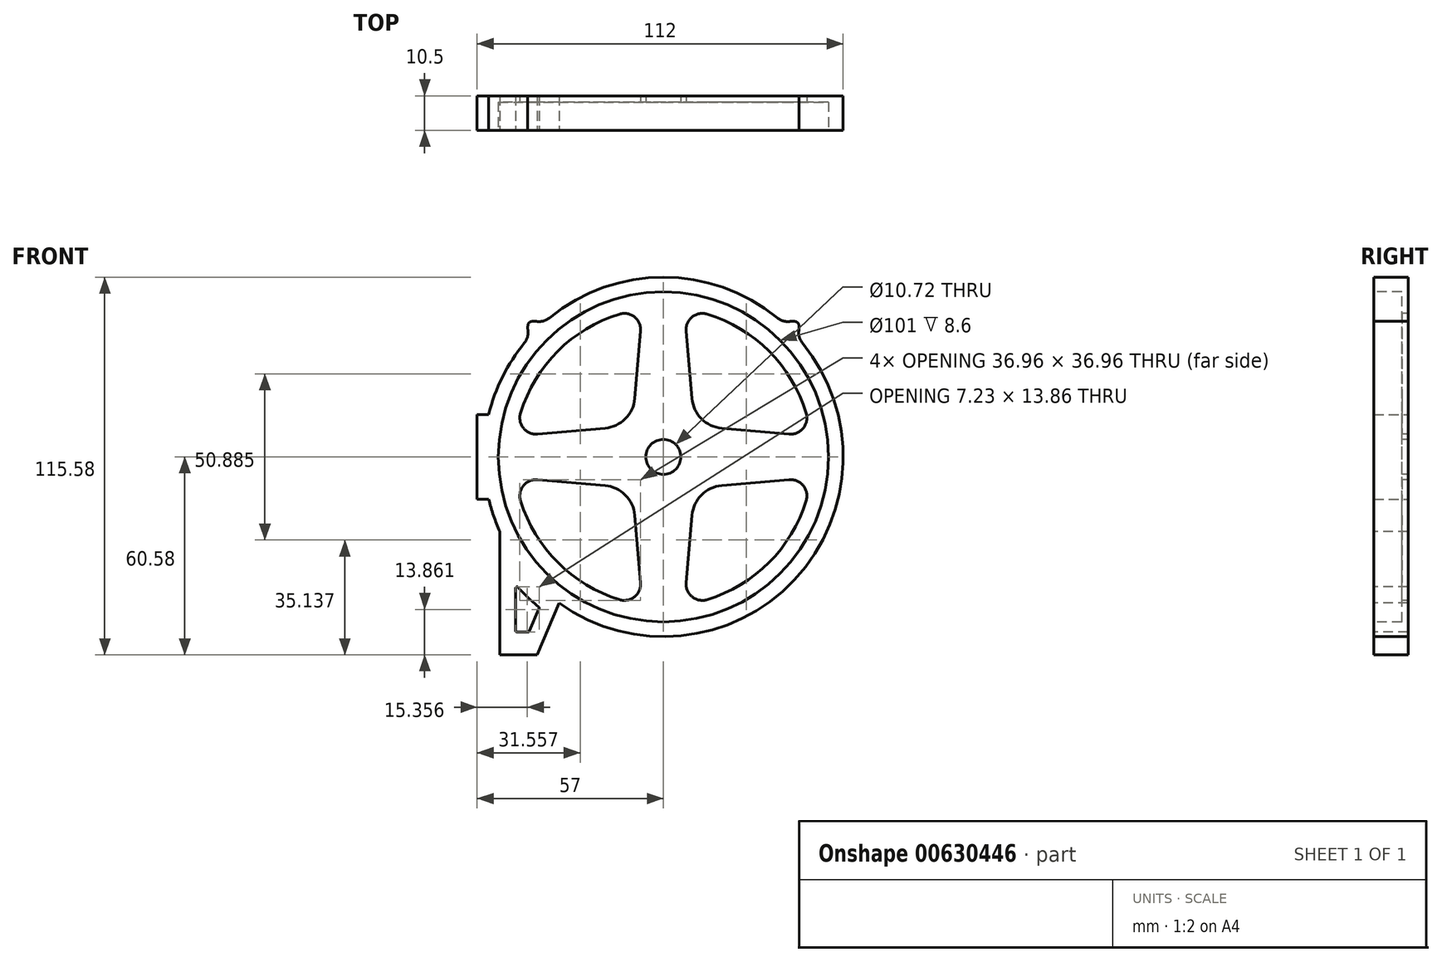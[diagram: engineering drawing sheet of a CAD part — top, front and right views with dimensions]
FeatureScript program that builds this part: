
annotation { "Feature Type Name" : "Feature", "Feature Type Description" : "" }
export const myFeature = defineFeature(function(context is Context, id is Id, definition is map)
    precondition{}
    {
        {
            var Q0;
            Q0=qCreatedBy(makeId("Front.planeOp"),FACE);
            var sketch = newSketch(context, id + "F0", { "sketchPlane" : qUnion([Q0])});
            skCircle(sketch, "E0", {"center": v(0, 0) * mm, "radius": 50.5 * mm});
            skArc(sketch, "E1", {"start": v(-53.44, -13) * mm, "mid": v(55, 0) * mm, "end": v(-53.44, 13) * mm});
            skLineSegment(sketch, "E2", {"start": v(0, 0) * mm, "end": v(55.3, 55.3) * mm});
            skLineSegment(sketch, "E3.trimOffspring", {"start": v(-38.9, 38.9) * mm, "end": v(-41.08, 41.08) * mm});
            skFitSpline(sketch, "E4", {"points": [v(-41.08, 36.57) * mm, v(-41.08, 41.08) * mm, v(-36.57, 41.08) * mm], "startDerivative": vector(-2.26, 11.29) * mm, "endDerivative": vector(11.29, -2.26) * mm});
            skFitSpline(sketch, "E5.MirrorCS", {"points": [v(41.08, 36.57) * mm, v(41.08, 41.08) * mm, v(36.57, 41.08) * mm], "startDerivative": vector(2.26, 11.29) * mm, "endDerivative": vector(-11.29, -2.26) * mm});
            skLineSegment(sketch, "E6.0", {"start": v(-57, -13) * mm, "end": v(-57, 0) * mm});
            skLineSegment(sketch, "E7.0", {"start": v(-57, 13) * mm, "end": v(-53.44, 13) * mm});
            skPoint(sketch, "E8.orphan", {"position": v(-50.5, 0) * mm});
            skLineSegment(sketch, "E9.MirrorCS", {"start": v(-57, -13) * mm, "end": v(-53.44, -13) * mm});
            skLineSegment(sketch, "E10", {"start": v(-57, 0) * mm, "end": v(-57, 13) * mm});
            skSolve(sketch);
        }
        {
            var Q0;
            Q0=makeQuery(id+"F0.imprint","IMPRINT",FACE,{"disambiguationData":[TD([[makeQuery(id+"F0.imprint","IMPRINT",EDGE,{"derivedFrom":sQuery(id+"F0.wireOp",EDGE,"E0")}),-1.0]])]});
            var Q1;
            {var subQ0=sQuery(id+"F0.wireOp",EDGE,"E3.trimOffspring");Q1=makeQuery(id+"F0.imprint","IMPRINT",FACE,{"disambiguationData":[TD([[makeQuery(id+"F0.imprint","IMPRINT",EDGE,{"derivedFrom":subQ0}),1.0]])]});}
            var Q2;
            {var subQ0=sQuery(id+"F0.wireOp",EDGE,"E3.trimOffspring");Q2=makeQuery(id+"F0.imprint","IMPRINT",FACE,{"disambiguationData":[TD([[makeQuery(id+"F0.imprint","IMPRINT",EDGE,{"derivedFrom":subQ0}),-1.0]])]});}
            var Q3;
            {var subQ0=sQuery(id+"F0.wireOp",EDGE,"E5.MirrorCS");var subQ1=sQuery(id+"F0.wireOp",EDGE,"E1");var subQ2=makeQuery(id+"F0.imprint","INTERSECT",VERTEX,{"disambiguationData":[OD(1.0)],"derivedFrom":[subQ1,subQ0]});Q3=makeQuery(id+"F0.imprint","IMPRINT",FACE,{"disambiguationData":[TD([[makeQuery(id+"F0.imprint","IMPRINT",EDGE,{"disambiguationData":[TD([[subQ2,1.0]])],"derivedFrom":subQ1}),-1.0]])]});}
            var Q4;
            {var subQ0=sQuery(id+"F0.wireOp",EDGE,"E5.MirrorCS");var subQ1=sQuery(id+"F0.wireOp",EDGE,"E1");var subQ2=makeQuery(id+"F0.imprint","INTERSECT",VERTEX,{"disambiguationData":[OD(0.0)],"derivedFrom":[subQ1,subQ0]});Q4=makeQuery(id+"F0.imprint","IMPRINT",FACE,{"disambiguationData":[TD([[makeQuery(id+"F0.imprint","IMPRINT",EDGE,{"disambiguationData":[TD([[subQ2,-1.0]])],"derivedFrom":subQ1}),-1.0]])]});}
            extrude(context, id + "F1", {"entities" : qUnion([Q0, Q1, Q2, Q3, Q4]), "depth" : 10.5 * mm, "offsetDistance" : 25 * mm});
        }
        {
            var Q0;
            {var subQ0=sQuery(id+"F0.wireOp",EDGE,"E4");var subQ1=sQuery(id+"F0.wireOp",EDGE,"E1");Q0=makeQuery(id+"F1.opExtrude","SWEPT_EDGE",EDGE,{"disambiguationData":[OSD([subQ1,subQ0]),TDD([makeQuery(id+"F0.imprint","INTERSECT",VERTEX,{"disambiguationData":[OD(0.0)],"derivedFrom":[subQ1,subQ0]})])]});}
            var Q1;
            {var subQ0=sQuery(id+"F0.wireOp",EDGE,"E4");var subQ1=sQuery(id+"F0.wireOp",EDGE,"E1");Q1=makeQuery(id+"F1.opExtrude","SWEPT_EDGE",EDGE,{"disambiguationData":[OSD([subQ1,subQ0]),TDD([makeQuery(id+"F0.imprint","INTERSECT",VERTEX,{"disambiguationData":[OD(1.0)],"derivedFrom":[subQ1,subQ0]})])]});}
            var Q2;
            {var subQ0=sQuery(id+"F0.wireOp",EDGE,"E5.MirrorCS");var subQ1=sQuery(id+"F0.wireOp",EDGE,"E1");Q2=makeQuery(id+"F1.opExtrude","SWEPT_EDGE",EDGE,{"disambiguationData":[OSD([subQ1,subQ0]),TDD([makeQuery(id+"F0.imprint","INTERSECT",VERTEX,{"disambiguationData":[OD(1.0)],"derivedFrom":[subQ1,subQ0]})])]});}
            var Q3;
            {var subQ0=sQuery(id+"F0.wireOp",EDGE,"E5.MirrorCS");var subQ1=sQuery(id+"F0.wireOp",EDGE,"E1");Q3=makeQuery(id+"F1.opExtrude","SWEPT_EDGE",EDGE,{"disambiguationData":[OSD([subQ1,subQ0]),TDD([makeQuery(id+"F0.imprint","INTERSECT",VERTEX,{"disambiguationData":[OD(0.0)],"derivedFrom":[subQ1,subQ0]})])]});}
            fillet(context, id + "F2", {"entities" : qUnion([Q0, Q1, Q2, Q3]), "radius" : 5 * mm, "tangentPropagation" : true, "allowEdgeOverflow" : false});
        }
        {
            var Q0;
            Q0=makeQuery(id+"F1.opExtrude","CAP_FACE",FACE,{"disambiguationData":[OSD([sQuery(id+"F0.wireOp",EDGE,"E0"),sQuery(id+"F0.wireOp",EDGE,"E1"),sQuery(id+"F0.wireOp",EDGE,"E4"),sQuery(id+"F0.wireOp",EDGE,"E5.MirrorCS"),sQuery(id+"F0.wireOp",EDGE,"E6.0"),sQuery(id+"F0.wireOp",EDGE,"E7.0"),sQuery(id+"F0.wireOp",EDGE,"E9.MirrorCS"),sQuery(id+"F0.wireOp",EDGE,"E10")])],"isStart":false});
            var sketch = newSketch(context, id + "F3", { "sketchPlane" : qUnion([Q0])});
            skCircle(sketch, "E11", {"center": v(0, 0) * mm, "radius": 5.36 * mm});
            skSolve(sketch);
        }
        {
            var Q0;
            Q0=makeQuery(id+"F3.imprint","IMPRINT",FACE,{"disambiguationData":[TD([[makeQuery(id+"F3.imprint","IMPRINT",EDGE,{"derivedFrom":sQuery(id+"F3.wireOp",EDGE,"E11")}),-1.0]])]});
            var Q1;
            Q1=makeQuery(id+"F1.opExtrude","CAP_FACE",FACE,{"disambiguationData":[OSD([sQuery(id+"F0.wireOp",EDGE,"E0"),sQuery(id+"F0.wireOp",EDGE,"E1"),sQuery(id+"F0.wireOp",EDGE,"E4"),sQuery(id+"F0.wireOp",EDGE,"E5.MirrorCS"),sQuery(id+"F0.wireOp",EDGE,"E6.0"),sQuery(id+"F0.wireOp",EDGE,"E7.0"),sQuery(id+"F0.wireOp",EDGE,"E9.MirrorCS"),sQuery(id+"F0.wireOp",EDGE,"E10")])],"isStart":true});
            extrude(context, id + "F4", {"entities" : qUnion([Q0]), "operationType" : NewBodyOperationType.ADD, "endBound" : BoundingType.UP_TO_SURFACE, "oppositeDirection" : true, "depth" : 25 * mm, "endBoundEntityFace" : qUnion([Q1]), "offsetDistance" : 25 * mm});
        }
        {
            var Q0;
            {var subQ0=sQuery(id+"F0.wireOp",EDGE,"E0");Q0=makeQuery(id+"F4.boolean.opBoolean","MERGE",FACE,{"derivedFrom":[makeQuery(id+"F1.opExtrude","CAP_FACE",FACE,{"disambiguationData":[OSD([subQ0,sQuery(id+"F0.wireOp",EDGE,"E1"),sQuery(id+"F0.wireOp",EDGE,"E4"),sQuery(id+"F0.wireOp",EDGE,"E5.MirrorCS"),sQuery(id+"F0.wireOp",EDGE,"E6.0"),sQuery(id+"F0.wireOp",EDGE,"E7.0"),sQuery(id+"F0.wireOp",EDGE,"E9.MirrorCS"),sQuery(id+"F0.wireOp",EDGE,"E10")])],"isStart":false}),makeQuery(id+"F4.opExtrude","CAP_FACE",FACE,{"disambiguationData":[OSD([subQ0,sQuery(id+"F3.wireOp",EDGE,"E11")])],"isStart":true})]});}
            var sketch = newSketch(context, id + "F5", { "sketchPlane" : qUnion([Q0])});
            skLineSegment(sketch, "E12.0", {"start": v(-62, -18) * mm, "end": v(-57.24, -18) * mm});
            skLineSegment(sketch, "E12.1", {"start": v(-62, 18) * mm, "end": v(-62, -18) * mm});
            skArc(sketch, "E12.2", {"start": v(-57.24, -18) * mm, "mid": v(28.53, -52.78) * mm, "end": v(46.41, 38.03) * mm});
            skLineSegment(sketch, "E12.3", {"start": v(-57.24, 18) * mm, "end": v(-62, 18) * mm});
            skFitSpline(sketch, "E12.4", {"points": [v(45.99, 35.59) * mm, v(46.03, 35.82) * mm, v(46.13, 36.32) * mm, v(46.28, 37.12) * mm, v(46.41, 37.98) * mm, v(46.5, 38.93) * mm, v(46.53, 40) * mm, v(46.43, 41.08) * mm, v(46.17, 42.08) * mm, v(45.85, 42.9) * mm, v(45.44, 43.63) * mm, v(45, 44.2) * mm, v(44.62, 44.62) * mm, v(44.2, 45) * mm, v(43.63, 45.44) * mm, v(42.9, 45.85) * mm, v(42.08, 46.17) * mm, v(41.08, 46.43) * mm, v(40, 46.53) * mm, v(38.93, 46.5) * mm, v(37.98, 46.41) * mm, v(37.12, 46.28) * mm, v(36.32, 46.13) * mm, v(35.82, 46.03) * mm, v(35.59, 45.99) * mm]});
            skArc(sketch, "E12.5", {"start": v(38.03, 46.41) * mm, "mid": v(0, 60) * mm, "end": v(-38.03, 46.41) * mm});
            skFitSpline(sketch, "E12.6", {"points": [v(-35.59, 45.99) * mm, v(-35.82, 46.03) * mm, v(-36.32, 46.13) * mm, v(-37.12, 46.28) * mm, v(-37.98, 46.41) * mm, v(-38.93, 46.5) * mm, v(-40, 46.53) * mm, v(-41.08, 46.43) * mm, v(-42.08, 46.17) * mm, v(-42.9, 45.85) * mm, v(-43.63, 45.44) * mm, v(-44.2, 45) * mm, v(-44.62, 44.62) * mm, v(-45, 44.2) * mm, v(-45.44, 43.63) * mm, v(-45.85, 42.9) * mm, v(-46.17, 42.08) * mm, v(-46.43, 41.08) * mm, v(-46.53, 40) * mm, v(-46.5, 38.93) * mm, v(-46.41, 37.98) * mm, v(-46.28, 37.12) * mm, v(-46.13, 36.32) * mm, v(-46.03, 35.82) * mm, v(-45.99, 35.59) * mm]});
            skArc(sketch, "E12.7", {"start": v(-46.41, 38.03) * mm, "mid": v(-52.78, 28.53) * mm, "end": v(-57.24, 18) * mm});
            skFitSpline(sketch, "E13.4", {"points": [v(45.99, 35.59) * mm, v(46.03, 35.82) * mm, v(46.13, 36.32) * mm, v(46.28, 37.12) * mm, v(46.41, 37.98) * mm, v(46.5, 38.93) * mm, v(46.53, 40) * mm, v(46.43, 41.08) * mm, v(46.17, 42.08) * mm, v(45.85, 42.9) * mm, v(45.44, 43.63) * mm, v(45, 44.2) * mm, v(44.62, 44.62) * mm, v(44.2, 45) * mm, v(43.63, 45.44) * mm, v(42.9, 45.85) * mm, v(42.08, 46.17) * mm, v(41.08, 46.43) * mm, v(40, 46.53) * mm, v(38.93, 46.5) * mm, v(37.98, 46.41) * mm, v(37.12, 46.28) * mm, v(36.32, 46.13) * mm, v(35.82, 46.03) * mm, v(35.59, 45.99) * mm]});
            skFitSpline(sketch, "E13.6", {"points": [v(-35.59, 45.99) * mm, v(-35.82, 46.03) * mm, v(-36.32, 46.13) * mm, v(-37.12, 46.28) * mm, v(-37.98, 46.41) * mm, v(-38.93, 46.5) * mm, v(-40, 46.53) * mm, v(-41.08, 46.43) * mm, v(-42.08, 46.17) * mm, v(-42.9, 45.85) * mm, v(-43.63, 45.44) * mm, v(-44.2, 45) * mm, v(-44.62, 44.62) * mm, v(-45, 44.2) * mm, v(-45.44, 43.63) * mm, v(-45.85, 42.9) * mm, v(-46.17, 42.08) * mm, v(-46.43, 41.08) * mm, v(-46.53, 40) * mm, v(-46.5, 38.93) * mm, v(-46.41, 37.98) * mm, v(-46.28, 37.12) * mm, v(-46.13, 36.32) * mm, v(-46.03, 35.82) * mm, v(-45.99, 35.59) * mm]});
            skLineSegment(sketch, "E14", {"start": v(-9.5, 9.5) * mm, "end": v(-6.37, 45.27) * mm});
            skLineSegment(sketch, "E15", {"start": v(-9.5, 9.5) * mm, "end": v(-45.27, 6.37) * mm});
            skLineSegment(sketch, "E16.MirrorCS", {"start": v(9.5, 9.5) * mm, "end": v(45.27, 6.37) * mm});
            skLineSegment(sketch, "E17.MirrorCS", {"start": v(9.5, 9.5) * mm, "end": v(6.37, 45.27) * mm});
            skLineSegment(sketch, "E18.MirrorCS", {"start": v(-9.5, -9.5) * mm, "end": v(-6.37, -45.27) * mm});
            skLineSegment(sketch, "E19.MirrorCS", {"start": v(-9.5, -9.5) * mm, "end": v(-45.27, -6.37) * mm});
            skLineSegment(sketch, "E20.MirrorCS", {"start": v(9.5, -9.5) * mm, "end": v(45.27, -6.37) * mm});
            skLineSegment(sketch, "E21.MirrorCS", {"start": v(9.5, -9.5) * mm, "end": v(6.37, -45.27) * mm});
            skArc(sketch, "E22", {"start": v(-6.37, 45.27) * mm, "mid": v(-32.33, 32.33) * mm, "end": v(-45.27, 6.37) * mm});
            skArc(sketch, "E23.trimOffspring", {"start": v(-45.27, -6.37) * mm, "mid": v(-32.33, -32.33) * mm, "end": v(-6.37, -45.27) * mm});
            skArc(sketch, "E24.trimOffspring", {"start": v(45.27, 6.37) * mm, "mid": v(32.33, 32.33) * mm, "end": v(6.37, 45.27) * mm});
            skArc(sketch, "E25.trimOffspring", {"start": v(6.37, -45.27) * mm, "mid": v(32.33, -32.33) * mm, "end": v(45.27, -6.37) * mm});
            skSolve(sketch);
        }
        {
            var Q0;
            Q0=makeQuery(id+"F5.imprint","IMPRINT",FACE,{"disambiguationData":[TD([[makeQuery(id+"F5.imprint","IMPRINT",EDGE,{"derivedFrom":sQuery(id+"F5.wireOp",EDGE,"E14")}),1.0]])]});
            var Q1;
            Q1=makeQuery(id+"F5.imprint","IMPRINT",FACE,{"disambiguationData":[TD([[makeQuery(id+"F5.imprint","IMPRINT",EDGE,{"derivedFrom":sQuery(id+"F5.wireOp",EDGE,"E16.MirrorCS")}),1.0]])]});
            var Q2;
            Q2=makeQuery(id+"F5.imprint","IMPRINT",FACE,{"disambiguationData":[TD([[makeQuery(id+"F5.imprint","IMPRINT",EDGE,{"derivedFrom":sQuery(id+"F5.wireOp",EDGE,"E20.MirrorCS")}),-1.0]])]});
            var Q3;
            Q3=makeQuery(id+"F5.imprint","IMPRINT",FACE,{"disambiguationData":[TD([[makeQuery(id+"F5.imprint","IMPRINT",EDGE,{"derivedFrom":sQuery(id+"F5.wireOp",EDGE,"E18.MirrorCS")}),-1.0]])]});
            extrude(context, id + "F6", {"entities" : qUnion([Q0, Q1, Q2, Q3]), "operationType" : NewBodyOperationType.REMOVE, "oppositeDirection" : true, "depth" : 25 * mm, "offsetDistance" : 25 * mm});
        }
        {
            var Q0;
            Q0=makeQuery(id+"F6.boolean.opBoolean","COPY",EDGE,{"derivedFrom":makeQuery(id+"F6.opExtrude","SWEPT_EDGE",EDGE,{"disambiguationData":[OSD([sQuery(id+"F5.wireOp",EDGE,"E14"),sQuery(id+"F5.wireOp",EDGE,"E15")])]})});
            var Q1;
            Q1=makeQuery(id+"F6.boolean.opBoolean","COPY",EDGE,{"derivedFrom":makeQuery(id+"F6.opExtrude","SWEPT_EDGE",EDGE,{"disambiguationData":[OSD([sQuery(id+"F5.wireOp",EDGE,"E16.MirrorCS"),sQuery(id+"F5.wireOp",EDGE,"E17.MirrorCS")])]})});
            var Q2;
            Q2=makeQuery(id+"F6.boolean.opBoolean","COPY",EDGE,{"derivedFrom":makeQuery(id+"F6.opExtrude","SWEPT_EDGE",EDGE,{"disambiguationData":[OSD([sQuery(id+"F5.wireOp",EDGE,"E20.MirrorCS"),sQuery(id+"F5.wireOp",EDGE,"E21.MirrorCS")])]})});
            var Q3;
            Q3=makeQuery(id+"F6.boolean.opBoolean","COPY",EDGE,{"derivedFrom":makeQuery(id+"F6.opExtrude","SWEPT_EDGE",EDGE,{"disambiguationData":[OSD([sQuery(id+"F5.wireOp",EDGE,"E18.MirrorCS"),sQuery(id+"F5.wireOp",EDGE,"E19.MirrorCS")])]})});
            fillet(context, id + "F7", {"entities" : qUnion([Q0, Q1, Q2, Q3]), "radius" : 10 * mm, "tangentPropagation" : true, "allowEdgeOverflow" : false});
        }
        {
            var Q0;
            Q0=makeQuery(id+"F6.boolean.opBoolean","COPY",EDGE,{"derivedFrom":makeQuery(id+"F6.opExtrude","SWEPT_EDGE",EDGE,{"disambiguationData":[OSD([sQuery(id+"F5.wireOp",EDGE,"E14"),sQuery(id+"F5.wireOp",EDGE,"CS6FgwBy-gh8V-Gnub-AYJi-HNmCZ0d2RgII")])]})});
            var Q1;
            Q1=makeQuery(id+"F6.boolean.opBoolean","COPY",EDGE,{"derivedFrom":makeQuery(id+"F6.opExtrude","SWEPT_EDGE",EDGE,{"disambiguationData":[OSD([sQuery(id+"F5.wireOp",EDGE,"ba3f9e5f-3280-4d9b-ae66-53b8c50e958d0.MirrorCS"),sQuery(id+"F5.wireOp",EDGE,"E17.MirrorCS")])]})});
            var Q2;
            Q2=makeQuery(id+"F6.boolean.opBoolean","COPY",EDGE,{"derivedFrom":makeQuery(id+"F6.opExtrude","SWEPT_EDGE",EDGE,{"disambiguationData":[OSD([sQuery(id+"F5.wireOp",EDGE,"E15"),sQuery(id+"F5.wireOp",EDGE,"CS6FgwBy-gh8V-Gnub-AYJi-HNmCZ0d2RgII")])]})});
            var Q3;
            Q3=makeQuery(id+"F6.boolean.opBoolean","COPY",EDGE,{"derivedFrom":makeQuery(id+"F6.opExtrude","SWEPT_EDGE",EDGE,{"disambiguationData":[OSD([sQuery(id+"F5.wireOp",EDGE,"ba3f9e5f-3280-4d9b-ae66-53b8c50e958d0.MirrorCS"),sQuery(id+"F5.wireOp",EDGE,"E16.MirrorCS")])]})});
            var Q4;
            Q4=makeQuery(id+"F6.boolean.opBoolean","COPY",EDGE,{"derivedFrom":makeQuery(id+"F6.opExtrude","SWEPT_EDGE",EDGE,{"disambiguationData":[OSD([sQuery(id+"F5.wireOp",EDGE,"E20.MirrorCS"),sQuery(id+"F5.wireOp",EDGE,"499c166e-646d-4cd2-add6-bc73e11a8d360.MirrorCS")])]})});
            var Q5;
            Q5=makeQuery(id+"F6.boolean.opBoolean","COPY",EDGE,{"derivedFrom":makeQuery(id+"F6.opExtrude","SWEPT_EDGE",EDGE,{"disambiguationData":[OSD([sQuery(id+"F5.wireOp",EDGE,"E21.MirrorCS"),sQuery(id+"F5.wireOp",EDGE,"499c166e-646d-4cd2-add6-bc73e11a8d360.MirrorCS")])]})});
            var Q6;
            Q6=makeQuery(id+"F6.boolean.opBoolean","COPY",EDGE,{"derivedFrom":makeQuery(id+"F6.opExtrude","SWEPT_EDGE",EDGE,{"disambiguationData":[OSD([sQuery(id+"F5.wireOp",EDGE,"f1b2ce39-3cac-499a-a383-90664cea46450.MirrorCS"),sQuery(id+"F5.wireOp",EDGE,"E19.MirrorCS")])]})});
            var Q7;
            Q7=makeQuery(id+"F6.boolean.opBoolean","COPY",EDGE,{"derivedFrom":makeQuery(id+"F6.opExtrude","SWEPT_EDGE",EDGE,{"disambiguationData":[OSD([sQuery(id+"F5.wireOp",EDGE,"f1b2ce39-3cac-499a-a383-90664cea46450.MirrorCS"),sQuery(id+"F5.wireOp",EDGE,"E18.MirrorCS")])]})});
            fillet(context, id + "F8", {"entities" : qUnion([Q0, Q1, Q2, Q3, Q4, Q5, Q6, Q7]), "radius" : 5 * mm, "tangentPropagation" : true, "allowEdgeOverflow" : false});
        }
        {
            var Q0;
            {var subQ0=sQuery(id+"F0.wireOp",EDGE,"E0");Q0=makeQuery(id+"F4.boolean.opBoolean","MERGE",FACE,{"derivedFrom":[makeQuery(id+"F1.opExtrude","CAP_FACE",FACE,{"disambiguationData":[OSD([subQ0,sQuery(id+"F0.wireOp",EDGE,"E1"),sQuery(id+"F0.wireOp",EDGE,"E4"),sQuery(id+"F0.wireOp",EDGE,"E5.MirrorCS"),sQuery(id+"F0.wireOp",EDGE,"E6.0"),sQuery(id+"F0.wireOp",EDGE,"E7.0"),sQuery(id+"F0.wireOp",EDGE,"E9.MirrorCS"),sQuery(id+"F0.wireOp",EDGE,"E10")])],"isStart":false}),makeQuery(id+"F4.opExtrude","CAP_FACE",FACE,{"disambiguationData":[OSD([subQ0,sQuery(id+"F3.wireOp",EDGE,"E11")])],"isStart":true})]});}
            var sketch = newSketch(context, id + "F9", { "sketchPlane" : qUnion([Q0])});
            skCircle(sketch, "E26", {"center": v(0, 0) * mm, "radius": 50.5 * mm});
            skSolve(sketch);
        }
        {
            var Q0;
            Q0=makeQuery(id+"F9.imprint","IMPRINT",FACE,{"disambiguationData":[TD([[makeQuery(id+"F9.imprint","IMPRINT",EDGE,{"derivedFrom":sQuery(id+"F9.wireOp",EDGE,"E26")}),1.0]])]});
            extrude(context, id + "F10", {"entities" : qUnion([Q0]), "operationType" : NewBodyOperationType.REMOVE, "oppositeDirection" : true, "depth" : 8.6 * mm, "offsetDistance" : 25 * mm});
        }
        {
            var Q0;
            {var subQ0=sQuery(id+"F0.wireOp",EDGE,"E0");Q0=makeQuery(id+"F4.boolean.opBoolean","MERGE",FACE,{"derivedFrom":[makeQuery(id+"F1.opExtrude","CAP_FACE",FACE,{"disambiguationData":[OSD([subQ0,sQuery(id+"F0.wireOp",EDGE,"E1"),sQuery(id+"F0.wireOp",EDGE,"E4"),sQuery(id+"F0.wireOp",EDGE,"E5.MirrorCS"),sQuery(id+"F0.wireOp",EDGE,"E6.0"),sQuery(id+"F0.wireOp",EDGE,"E7.0"),sQuery(id+"F0.wireOp",EDGE,"E9.MirrorCS"),sQuery(id+"F0.wireOp",EDGE,"E10")])],"isStart":false}),makeQuery(id+"F4.opExtrude","CAP_FACE",FACE,{"disambiguationData":[OSD([subQ0,sQuery(id+"F3.wireOp",EDGE,"E11")])],"isStart":true})]});}
            var sketch = newSketch(context, id + "F11", { "sketchPlane" : qUnion([Q0])});
            skLineSegment(sketch, "E27.0", {"start": v(-50, -22.91) * mm, "end": v(-50, -60.58) * mm});
            skArc(sketch, "E28.0", {"start": v(-50, -22.91) * mm, "mid": v(29.12, -46.66) * mm, "end": v(42.54, 34.86) * mm});
            skPoint(sketch, "E29.orphan", {"position": v(-53.44, -13) * mm});
            skLineSegment(sketch, "E30", {"start": v(-38.64, -60.58) * mm, "end": v(-31.94, -44.77) * mm});
            skLineSegment(sketch, "E31.trimOffspring", {"start": v(-38.64, -60.58) * mm, "end": v(-50, -60.58) * mm});
            skSolve(sketch);
        }
        {
            var Q0;
            {var subQ0=sQuery(id+"F11.wireOp",EDGE,"E27.0");Q0=makeQuery(id+"F11.imprint","IMPRINT",FACE,{"disambiguationData":[TD([[makeQuery(id+"F11.imprint","IMPRINT",EDGE,{"derivedFrom":subQ0}),1.0]])]});}
            var Q1;
            {var subQ0=sQuery(id+"F0.wireOp",EDGE,"E10");var subQ1=sQuery(id+"F0.wireOp",EDGE,"E9.MirrorCS");var subQ2=sQuery(id+"F0.wireOp",EDGE,"E7.0");var subQ3=sQuery(id+"F0.wireOp",EDGE,"E6.0");var subQ4=sQuery(id+"F0.wireOp",EDGE,"E5.MirrorCS");var subQ5=sQuery(id+"F0.wireOp",EDGE,"E4");var subQ6=sQuery(id+"F0.wireOp",EDGE,"E1");var subQ7=sQuery(id+"F0.wireOp",EDGE,"E0");Q1=makeQuery(id+"F4.boolean.opBoolean","MERGE",FACE,{"derivedFrom":[makeQuery(id+"F1.opExtrude","CAP_FACE",FACE,{"disambiguationData":[OSD([subQ7,subQ6,subQ5,subQ4,subQ3,subQ2,subQ1,subQ0])],"isStart":true}),makeQuery(id+"F4.opExtrude","CAP_FACE",FACE,{"disambiguationData":[OSD([subQ7,subQ6,subQ5,subQ4,subQ3,subQ2,subQ1,subQ0])],"isStart":false})]});}
            extrude(context, id + "F12", {"entities" : qUnion([Q0]), "operationType" : NewBodyOperationType.ADD, "endBound" : BoundingType.UP_TO_SURFACE, "oppositeDirection" : true, "depth" : 25 * mm, "endBoundEntityFace" : qUnion([Q1]), "offsetDistance" : 25 * mm});
        }
        {
            var Q0;
            {var subQ0=sQuery(id+"F11.wireOp",EDGE,"E31.trimOffspring");var subQ1=sQuery(id+"F11.wireOp",EDGE,"E30");var subQ2=sQuery(id+"F11.wireOp",EDGE,"E28.0");var subQ3=sQuery(id+"F11.wireOp",EDGE,"E27.0");var subQ4=sQuery(id+"F0.wireOp",EDGE,"E0");Q0=makeQuery(id+"FEUEAjGLeRdBD8V_1.1.F12.boolean.opBoolean","MERGE",FACE,{"derivedFrom":[makeQuery(id+"F12.boolean.opBoolean","MERGE",FACE,{"derivedFrom":[makeQuery(id+"F4.boolean.opBoolean","MERGE",FACE,{"derivedFrom":[makeQuery(id+"F1.opExtrude","CAP_FACE",FACE,{"disambiguationData":[OSD([subQ4,sQuery(id+"F0.wireOp",EDGE,"E1"),sQuery(id+"F0.wireOp",EDGE,"E4"),sQuery(id+"F0.wireOp",EDGE,"E5.MirrorCS"),sQuery(id+"F0.wireOp",EDGE,"E6.0"),sQuery(id+"F0.wireOp",EDGE,"E7.0"),sQuery(id+"F0.wireOp",EDGE,"E9.MirrorCS"),sQuery(id+"F0.wireOp",EDGE,"E10")])],"isStart":false}),makeQuery(id+"F4.opExtrude","CAP_FACE",FACE,{"disambiguationData":[OSD([subQ4,sQuery(id+"F3.wireOp",EDGE,"E11")])],"isStart":true})]}),makeQuery(id+"F12.opExtrude","CAP_FACE",FACE,{"disambiguationData":[OSD([subQ3,subQ2,subQ1,subQ0])],"isStart":true})]}),makeQuery(id+"FEUEAjGLeRdBD8V_1.1.F12.opExtrude","CAP_FACE",FACE,{"disambiguationData":[OSD([subQ3,subQ2,subQ1,subQ0])],"isStart":true})]});}
            var sketch = newSketch(context, id + "F13", { "sketchPlane" : qUnion([Q0])});
            skArc(sketch, "E32", {"start": v(-44.39, -39.96) * mm, "mid": v(-41.4, -43.04) * mm, "end": v(-38.2, -45.9) * mm});
            skLineSegment(sketch, "E33", {"start": v(-45.26, -40.29) * mm, "end": v(-45.26, -53.15) * mm});
            skLineSegment(sketch, "E34", {"start": v(-44.76, -53.65) * mm, "end": v(-41.44, -53.65) * mm});
            skLineSegment(sketch, "E35", {"start": v(-40.98, -53.34) * mm, "end": v(-38.07, -46.48) * mm});
            skPoint(sketch, "E36.visualSharp", {"position": v(-45.26, -38.97) * mm});
            skArc(sketch, "E36.filletArc", {"start": v(-44.39, -39.96) * mm, "mid": v(-44.94, -39.82) * mm, "end": v(-45.26, -40.29) * mm});
            skPoint(sketch, "E37.visualSharp", {"position": v(-37.92, -46.14) * mm});
            skArc(sketch, "E37.filletArc", {"start": v(-38.07, -46.48) * mm, "mid": v(-38.04, -46.17) * mm, "end": v(-38.2, -45.9) * mm});
            skPoint(sketch, "E38.visualSharp", {"position": v(-41.1, -53.65) * mm});
            skArc(sketch, "E38.filletArc", {"start": v(-41.44, -53.65) * mm, "mid": v(-41.16, -53.56) * mm, "end": v(-40.98, -53.34) * mm});
            skPoint(sketch, "E39.visualSharp", {"position": v(-45.26, -53.65) * mm});
            skArc(sketch, "E39.filletArc", {"start": v(-45.26, -53.15) * mm, "mid": v(-45.11, -53.5) * mm, "end": v(-44.76, -53.65) * mm});
            skSolve(sketch);
        }
        {
            var Q0;
            Q0=makeQuery(id+"F13.imprint","IMPRINT",FACE,{"disambiguationData":[TD([[makeQuery(id+"F13.imprint","IMPRINT",EDGE,{"derivedFrom":sQuery(id+"F13.wireOp",EDGE,"E32")}),-1.0]])]});
            extrude(context, id + "F14", {"entities" : qUnion([Q0]), "operationType" : NewBodyOperationType.REMOVE, "endBound" : BoundingType.THROUGH_ALL, "oppositeDirection" : true, "depth" : 25 * mm, "offsetDistance" : 25 * mm});
        }
    });
